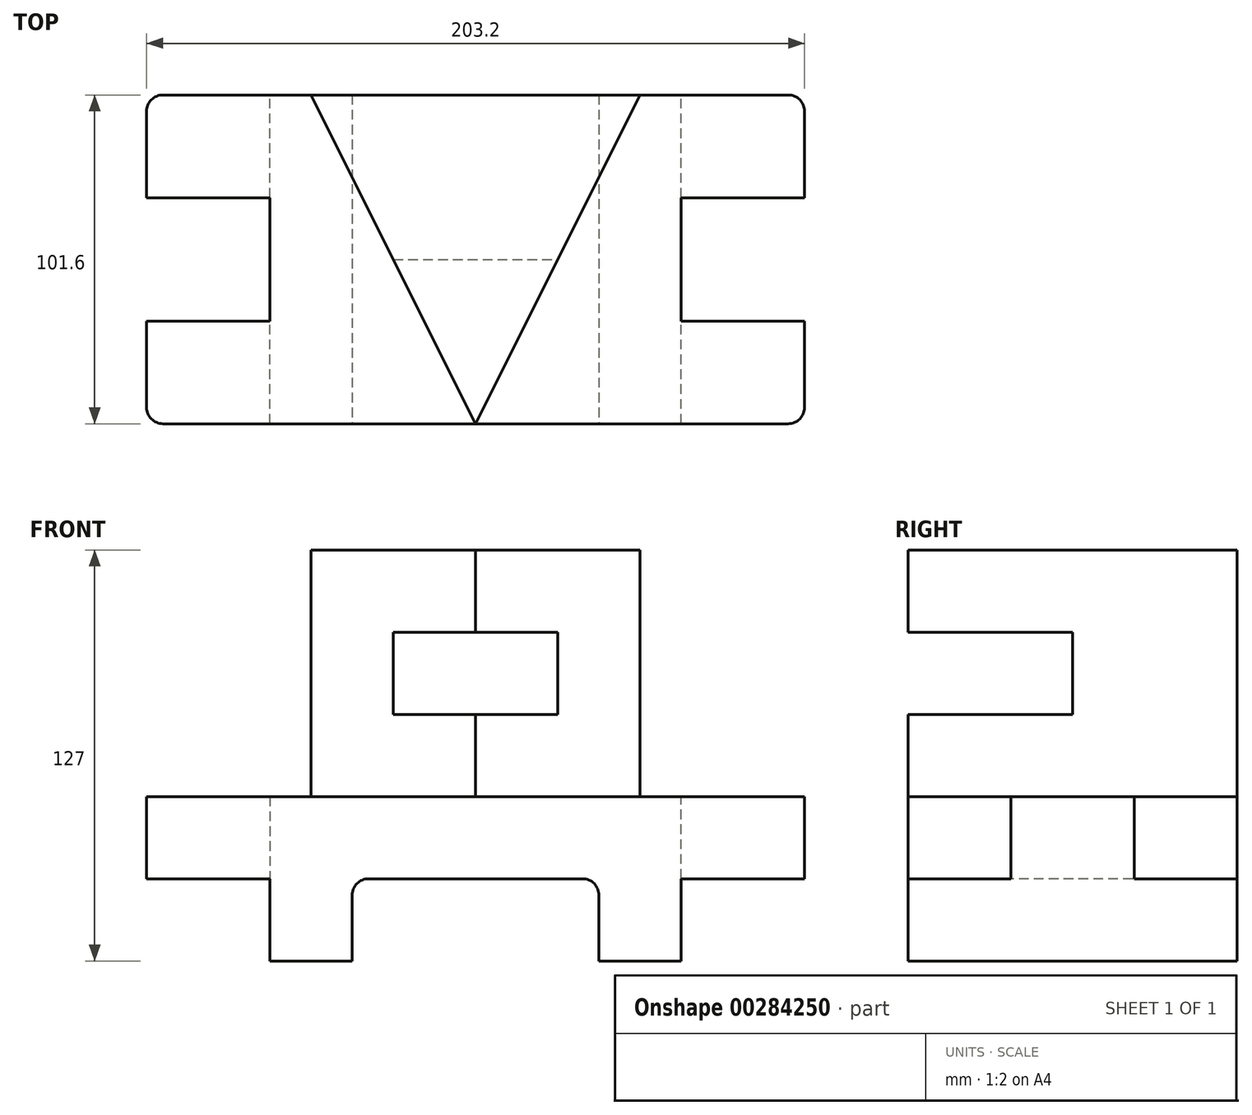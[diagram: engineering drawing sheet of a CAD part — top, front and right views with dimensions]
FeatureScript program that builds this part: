
annotation { "Feature Type Name" : "Feature", "Feature Type Description" : "" }
export const myFeature = defineFeature(function(context is Context, id is Id, definition is map)
    precondition{}
    {
        {
            var Q0;
            Q0=qCreatedBy(makeId("Front.planeOp"),FACE);
            var sketch = newSketch(context, id + "F0", { "sketchPlane" : qUnion([Q0])});
            skLineSegment(sketch, "E0.bottom", {"start": v(-101.6, 0) * mm, "end": v(101.6, 0) * mm});
            skLineSegment(sketch, "E0.top", {"start": v(-101.6, 25.4) * mm, "end": v(101.6, 25.4) * mm});
            skLineSegment(sketch, "E0.left", {"start": v(-101.6, 0) * mm, "end": v(-101.6, 25.4) * mm});
            skLineSegment(sketch, "E0.right", {"start": v(101.6, 0) * mm, "end": v(101.6, 25.4) * mm});
            skSolve(sketch);
        }
        {
            var Q0;
            Q0 = qSketchRegion(id + "F0", true);
            extrude(context, id + "F1", {"entities" : qUnion([Q0]), "endBound" : BoundingType.SYMMETRIC, "depth" : 101.6 * mm});
        }
        {
            var Q0;
            Q0=makeQuery(id+"F1.opExtrude","CAP_EDGE",EDGE,{"disambiguationData":[OSD([sQuery(id+"F0.wireOp",EDGE,"E0.right")])],"isStart":false});
            var Q1;
            Q1=makeQuery(id+"F1.opExtrude","CAP_EDGE",EDGE,{"disambiguationData":[OSD([sQuery(id+"F0.wireOp",EDGE,"E0.right")])],"isStart":true});
            var Q2;
            Q2=makeQuery(id+"F1.opExtrude","CAP_EDGE",EDGE,{"disambiguationData":[OSD([sQuery(id+"F0.wireOp",EDGE,"E0.left")])],"isStart":false});
            var Q3;
            Q3=makeQuery(id+"F1.opExtrude","CAP_EDGE",EDGE,{"disambiguationData":[OSD([sQuery(id+"F0.wireOp",EDGE,"E0.left")])],"isStart":true});
            fillet(context, id + "F2", {"entities" : qUnion([Q0, Q1, Q2, Q3]), "radius" : 5.08 * mm, "tangentPropagation" : true, "allowEdgeOverflow" : false});
        }
        {
            var Q0;
            Q0=makeQuery(id+"F1.opExtrude","SWEPT_FACE",FACE,{"disambiguationData":[OSD([sQuery(id+"F0.wireOp",EDGE,"E0.top")])]});
            var sketch = newSketch(context, id + "F3", { "sketchPlane" : qUnion([Q0])});
            skLineSegment(sketch, "E1", {"start": v(-50.8, 50.8) * mm, "end": v(50.8, 50.8) * mm});
            skLineSegment(sketch, "E2", {"start": v(-50.8, 50.8) * mm, "end": v(0, -50.8) * mm});
            skLineSegment(sketch, "E3", {"start": v(0, -50.8) * mm, "end": v(50.8, 50.8) * mm});
            skSolve(sketch);
        }
        {
            var Q0;
            Q0 = qSketchRegion(id + "F3", true);
            extrude(context, id + "F4", {"entities" : qUnion([Q0]), "operationType" : NewBodyOperationType.ADD, "depth" : 76.2 * mm});
        }
        {
            var Q0;
            Q0=qCreatedBy(makeId("Right.planeOp"),FACE);
            var sketch = newSketch(context, id + "F5", { "sketchPlane" : qUnion([Q0])});
            skLineSegment(sketch, "E4.bottom", {"start": v(-50.8, 0) * mm, "end": v(50.8, 0) * mm});
            skLineSegment(sketch, "E4.top", {"start": v(-50.8, -25.4) * mm, "end": v(50.8, -25.4) * mm});
            skLineSegment(sketch, "E4.left", {"start": v(-50.8, 0) * mm, "end": v(-50.8, -25.4) * mm});
            skLineSegment(sketch, "E4.right", {"start": v(50.8, 0) * mm, "end": v(50.8, -25.4) * mm});
            skSolve(sketch);
        }
        {
            var Q0;
            Q0 = qSketchRegion(id + "F5", true);
            extrude(context, id + "F6", {"entities" : qUnion([Q0]), "operationType" : NewBodyOperationType.ADD, "endBound" : BoundingType.SYMMETRIC, "depth" : 127 * mm});
        }
        {
            var Q0;
            Q0=qCreatedBy(makeId("Front.planeOp"),FACE);
            var sketch = newSketch(context, id + "F7", { "sketchPlane" : qUnion([Q0])});
            skLineSegment(sketch, "E5.bottom", {"start": v(-25.4, 76.2) * mm, "end": v(25.4, 76.2) * mm});
            skLineSegment(sketch, "E5.top", {"start": v(-25.4, 50.8) * mm, "end": v(25.4, 50.8) * mm});
            skLineSegment(sketch, "E5.left", {"start": v(-25.4, 76.2) * mm, "end": v(-25.4, 50.8) * mm});
            skLineSegment(sketch, "E5.right", {"start": v(25.4, 76.2) * mm, "end": v(25.4, 50.8) * mm});
            skSolve(sketch);
        }
        {
            var Q0;
            Q0 = qSketchRegion(id + "F7", true);
            extrude(context, id + "F8", {"entities" : qUnion([Q0]), "operationType" : NewBodyOperationType.REMOVE, "endBound" : BoundingType.THROUGH_ALL, "depth" : 154.18 * mm});
        }
        {
            var Q0;
            Q0=makeQuery(id+"F1.opExtrude","SWEPT_FACE",FACE,{"disambiguationData":[OSD([sQuery(id+"F0.wireOp",EDGE,"E0.right")])]});
            var sketch = newSketch(context, id + "F9", { "sketchPlane" : qUnion([Q0])});
            skLineSegment(sketch, "E6.bottom", {"start": v(19.05, 0) * mm, "end": v(-19.05, 0) * mm});
            skLineSegment(sketch, "E6.top", {"start": v(19.05, 25.4) * mm, "end": v(-19.05, 25.4) * mm});
            skLineSegment(sketch, "E6.left", {"start": v(19.05, 0) * mm, "end": v(19.05, 25.4) * mm});
            skLineSegment(sketch, "E6.right", {"start": v(-19.05, 0) * mm, "end": v(-19.05, 25.4) * mm});
            skSolve(sketch);
        }
        {
            var Q0;
            Q0 = qSketchRegion(id + "F9", true);
            extrude(context, id + "F10", {"entities" : qUnion([Q0]), "operationType" : NewBodyOperationType.REMOVE, "oppositeDirection" : true, "depth" : 38.1 * mm});
        }
        {
            var Q0;
            Q0=makeQuery(id+"F1.opExtrude","SWEPT_FACE",FACE,{"disambiguationData":[OSD([sQuery(id+"F0.wireOp",EDGE,"E0.left")])]});
            var sketch = newSketch(context, id + "F11", { "sketchPlane" : qUnion([Q0])});
            skLineSegment(sketch, "E7.bottom", {"start": v(-19.05, 25.4) * mm, "end": v(19.05, 25.4) * mm});
            skLineSegment(sketch, "E7.top", {"start": v(-19.05, 0) * mm, "end": v(19.05, 0) * mm});
            skLineSegment(sketch, "E7.left", {"start": v(-19.05, 25.4) * mm, "end": v(-19.05, 0) * mm});
            skLineSegment(sketch, "E7.right", {"start": v(19.05, 25.4) * mm, "end": v(19.05, 0) * mm});
            skSolve(sketch);
        }
        {
            var Q0;
            Q0 = qSketchRegion(id + "F11", true);
            extrude(context, id + "F12", {"entities" : qUnion([Q0]), "operationType" : NewBodyOperationType.REMOVE, "oppositeDirection" : true, "depth" : 38.1 * mm});
        }
        {
            var Q0;
            Q0=makeQuery(id+"F6.boolean.opBoolean","MERGE",FACE,{"derivedFrom":[makeQuery(id+"F1.opExtrude","CAP_FACE",FACE,{"disambiguationData":[OSD([sQuery(id+"F0.wireOp",EDGE,"E0.bottom"),sQuery(id+"F0.wireOp",EDGE,"E0.top"),sQuery(id+"F0.wireOp",EDGE,"E0.left"),sQuery(id+"F0.wireOp",EDGE,"E0.right")])],"isStart":false}),makeQuery(id+"F6.opExtrude","SWEPT_FACE",FACE,{"disambiguationData":[OSD([sQuery(id+"F5.wireOp",EDGE,"E4.left")])]})]});
            var sketch = newSketch(context, id + "F13", { "sketchPlane" : qUnion([Q0])});
            skLineSegment(sketch, "E8.bottom", {"start": v(-38.1, 0) * mm, "end": v(38.1, 0) * mm});
            skLineSegment(sketch, "E8.top", {"start": v(-38.1, -25.4) * mm, "end": v(38.1, -25.4) * mm});
            skLineSegment(sketch, "E8.left", {"start": v(-38.1, 0) * mm, "end": v(-38.1, -25.4) * mm});
            skLineSegment(sketch, "E8.right", {"start": v(38.1, 0) * mm, "end": v(38.1, -25.4) * mm});
            skSolve(sketch);
        }
        {
            var Q0;
            Q0 = qSketchRegion(id + "F13", true);
            extrude(context, id + "F14", {"entities" : qUnion([Q0]), "operationType" : NewBodyOperationType.REMOVE, "endBound" : BoundingType.THROUGH_ALL, "oppositeDirection" : true, "depth" : 25.4 * mm});
        }
        {
            var Q0;
            Q0=makeQuery(id+"F14.boolean.opBoolean","COPY",EDGE,{"derivedFrom":makeQuery(id+"F14.opExtrude","SWEPT_EDGE",EDGE,{"disambiguationData":[OSD([sQuery(id+"F13.wireOp",EDGE,"E8.bottom"),sQuery(id+"F13.wireOp",EDGE,"E8.left")])]})});
            var Q1;
            Q1=makeQuery(id+"F14.boolean.opBoolean","COPY",EDGE,{"derivedFrom":makeQuery(id+"F14.opExtrude","SWEPT_EDGE",EDGE,{"disambiguationData":[OSD([sQuery(id+"F13.wireOp",EDGE,"E8.bottom"),sQuery(id+"F13.wireOp",EDGE,"E8.right")])]})});
            fillet(context, id + "F15", {"entities" : qUnion([Q0, Q1]), "radius" : 5.08 * mm, "tangentPropagation" : true, "allowEdgeOverflow" : false});
        }
    });
